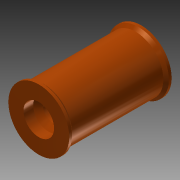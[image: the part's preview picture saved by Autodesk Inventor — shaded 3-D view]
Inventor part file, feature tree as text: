
AUTODESK INVENTOR PART (.ipt)
format: ipt  version: 2013 (Build 170138000, 138)  size: 136,192 bytes
history: native  units: mm
features: sketch x5, extrude x4, chamfer x2, revolve x1, projected_geometry x1
ambient origin geometry x8: Origin, YZ Plane, XZ Plane, XY Plane, X Axis, Y Axis, Z Axis, Center Point
bodies: Solid1 (feature_tree)
feature tree (13):
  revolve  "Revolution1"  [1 undecoded]
  chamfer  "Chamfer1"  Distance=2.0mm Angle=45.0deg
  extrude  "Extrusion1"  Depth=56.0mm TaperAngle=0.0deg
  extrude  "Extrusion2"  Depth=7.0mm TaperAngle=0.0deg
  extrude  "Extrusion3"  Depth=15.1mm
  chamfer  "Chamfer2"  Distance=7.0mm
  extrude  "Extrusion4"  Depth=3.5mm TaperAngle=45.0deg
  sketch  "Sketch1"  dims[d0=22.0mm d5=70.0mm]
  sketch  "Sketch2"  dims[d6=2.0mm]
  sketch  "Sketch3"  dims[d7=2.0mm]
  projected_geometry  "Projected Loop1"
  sketch  "Sketch4"  dims[d8=90.0deg d9=2.0mm d10=2.0mm d11=45.0deg]
  sketch  "Sketch5"  dims[d12=22.1mm d14=56.0mm d15=0.0mm d16=7.0mm d17=0.0mm d18=15.1mm d20=7.0mm d21=0.0mm d22=3.5mm d23=2.0mm d24=45.0deg d25=8.95mm d26=2.0mm d27=49.0mm d28=0.0mm d29=2.0mm]
note: 1 required parameter value undecoded (feature->parameter linkage not recoverable at this tier; creation-order binding heuristic only, values carry confidence <= 0.55)
